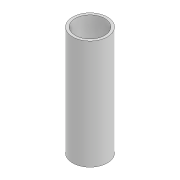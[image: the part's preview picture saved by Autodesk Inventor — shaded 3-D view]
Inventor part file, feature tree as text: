
AUTODESK INVENTOR PART (.ipt)
format: ipt  version: 2022 (Build 260153000, 153)  size: 78,848 bytes
history: native  units: mm
features: extrude x1, sketch x1
ambient origin geometry x8: Origin, YZ Plane, XZ Plane, XY Plane, X Axis, Y Axis, Z Axis, Center Point
bodies: Solid1 (feature_tree)
feature tree (2):
  extrude  "Extrusion1"  Depth=126.0mm
  sketch  "Sketch1"  dims[d0=40.0mm d1=3.0mm d2=126.0mm d3=0.0mm]
